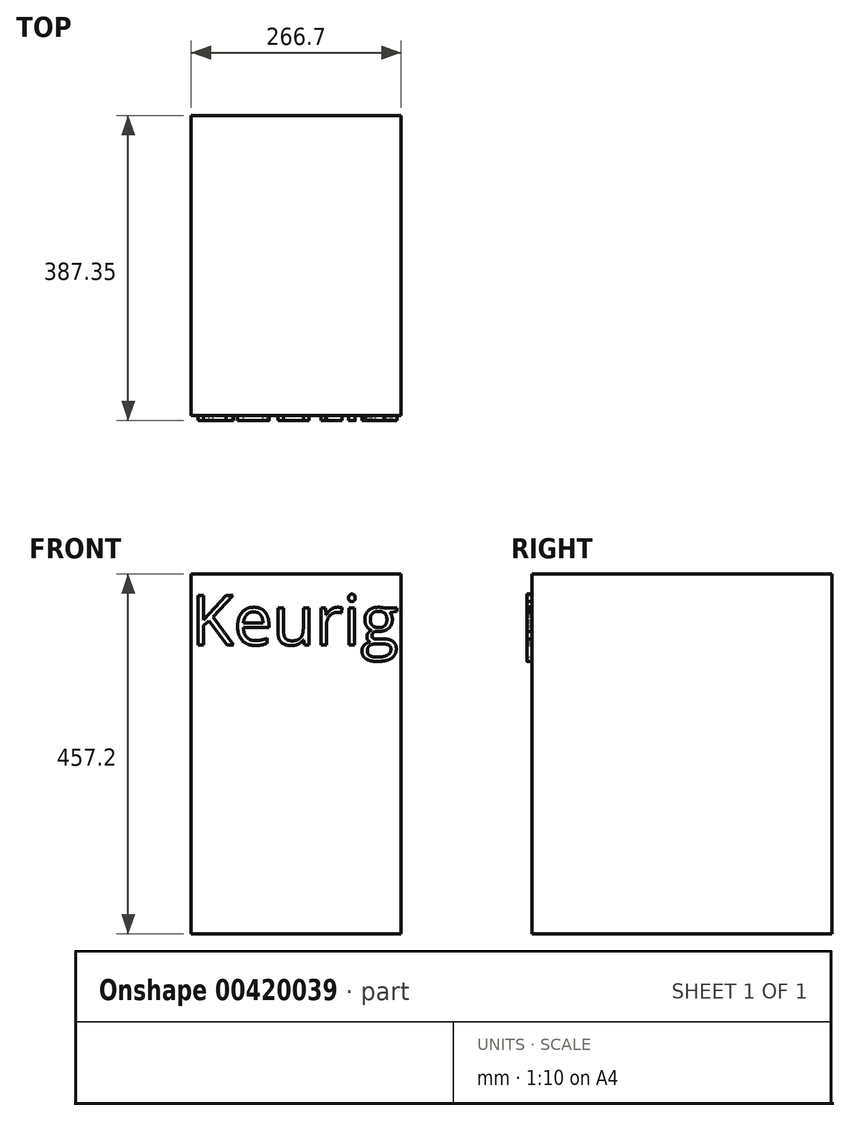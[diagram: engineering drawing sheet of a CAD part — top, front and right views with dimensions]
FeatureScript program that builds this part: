
annotation { "Feature Type Name" : "Feature", "Feature Type Description" : "" }
export const myFeature = defineFeature(function(context is Context, id is Id, definition is map)
    precondition{}
    {
        {
            var Q0;
            Q0=qCreatedBy(makeId("Front.planeOp"),FACE);
            var sketch = newSketch(context, id + "F0", { "sketchPlane" : qUnion([Q0])});
            skLineSegment(sketch, "E0.bottom", {"start": v(0, 0) * mm, "end": v(266.7, 0) * mm});
            skLineSegment(sketch, "E0.top", {"start": v(0, 457.2) * mm, "end": v(266.7, 457.2) * mm});
            skLineSegment(sketch, "E0.left", {"start": v(0, 0) * mm, "end": v(0, 457.2) * mm});
            skLineSegment(sketch, "E0.right", {"start": v(266.7, 0) * mm, "end": v(266.7, 457.2) * mm});
            skSolve(sketch);
        }
        {
            var Q0;
            Q0=makeQuery(id+"F0.imprint","IMPRINT",FACE,{"disambiguationData":[TD([[makeQuery(id+"F0.imprint","IMPRINT",EDGE,{"derivedFrom":sQuery(id+"F0.wireOp",EDGE,"E0.bottom")}),1.0]])]});
            extrude(context, id + "F1", {"entities" : qUnion([Q0]), "depth" : 381 * mm});
        }
        {
            var Q0;
            Q0=makeQuery(id+"F1.opExtrude","CAP_FACE",FACE,{"disambiguationData":[OSD([sQuery(id+"F0.wireOp",EDGE,"E0.bottom"),sQuery(id+"F0.wireOp",EDGE,"E0.top"),sQuery(id+"F0.wireOp",EDGE,"E0.left"),sQuery(id+"F0.wireOp",EDGE,"E0.right")])],"isStart":false});
            var sketch = newSketch(context, id + "F2", { "sketchPlane" : qUnion([Q0])});
            skText(sketch, "E1", { "text": "Keurig", "fontName": "OpenSans-Regular.ttf"});
            const initialGuessF2  = {"E1": [0, 0.3672, 1, 0, 0.0632]};
            skSetInitialGuess(sketch, initialGuessF2);
            skSolve(sketch);
        }
        {
            var Q0;
            Q0 = qSketchRegion(id + "F2", true);
            extrude(context, id + "F3", {"entities" : qUnion([Q0]), "operationType" : NewBodyOperationType.ADD, "depth" : 6.35 * mm});
        }
    });
